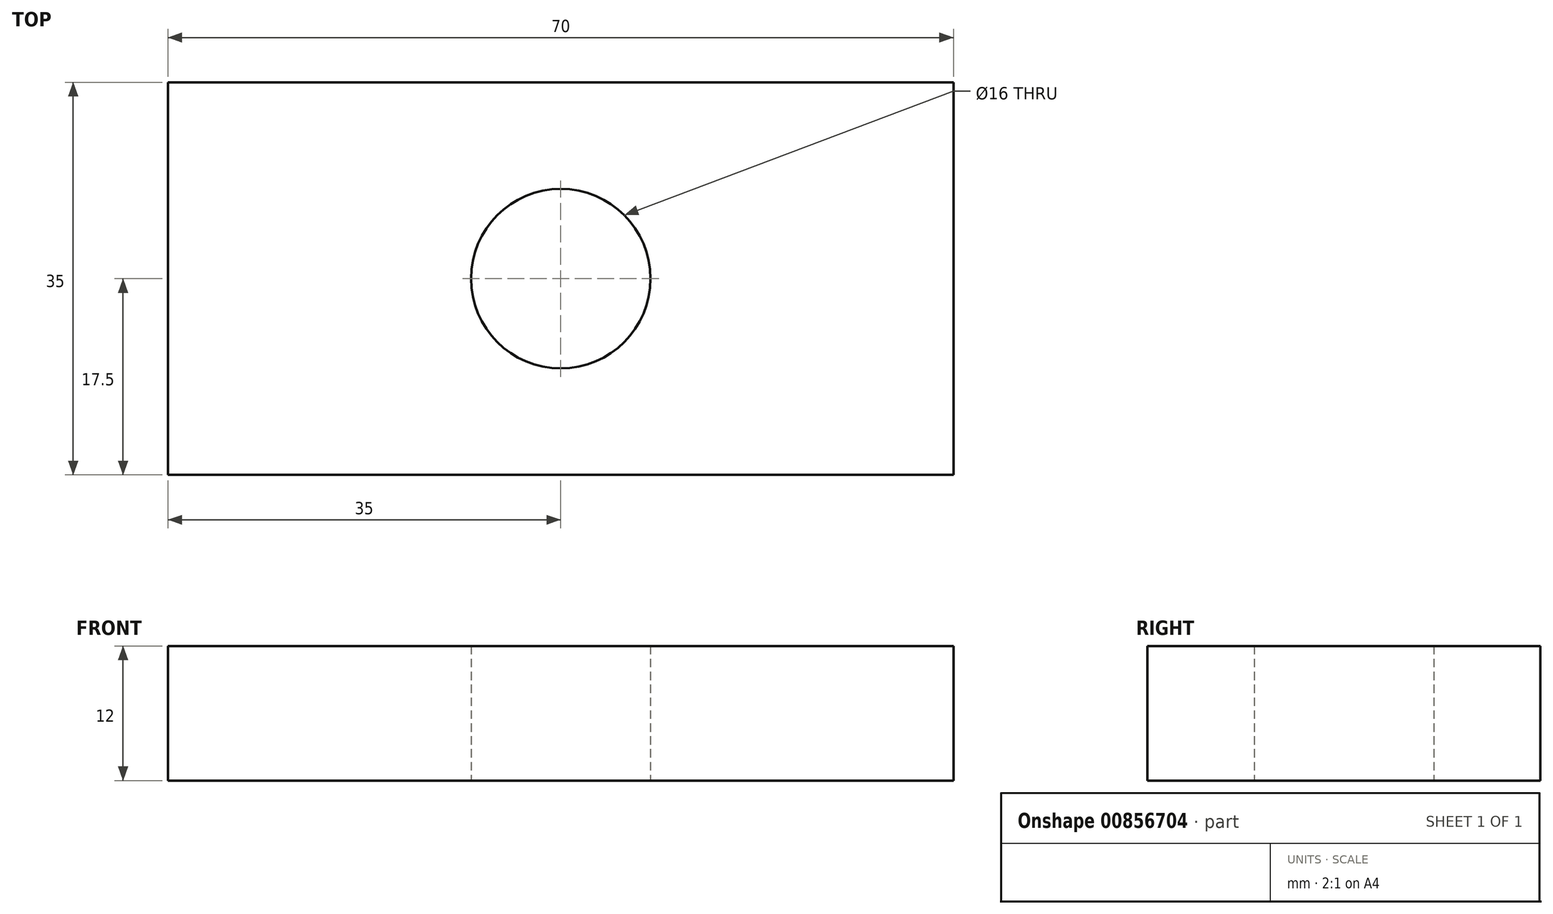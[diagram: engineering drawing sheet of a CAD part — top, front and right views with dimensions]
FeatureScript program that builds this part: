
annotation { "Feature Type Name" : "Feature", "Feature Type Description" : "" }
export const myFeature = defineFeature(function(context is Context, id is Id, definition is map)
    precondition{}
    {
        {
            var Q0;
            Q0=qCreatedBy(makeId("Top.planeOp"),FACE);
            var sketch = newSketch(context, id + "F0", { "sketchPlane" : qUnion([Q0])});
            skCircle(sketch, "E0", {"center": v(0, 0) * mm, "radius": 8 * mm});
            skLineSegment(sketch, "E1.bottom", {"start": v(-35, -17.5) * mm, "end": v(35, -17.5) * mm});
            skLineSegment(sketch, "E1.top", {"start": v(-35, 17.5) * mm, "end": v(35, 17.5) * mm});
            skLineSegment(sketch, "E1.left", {"start": v(-35, -17.5) * mm, "end": v(-35, 17.5) * mm});
            skLineSegment(sketch, "E1.right", {"start": v(35, -17.5) * mm, "end": v(35, 17.5) * mm});
            skLineSegment(sketch, "E2.bottom", {"start": v(-60, -25) * mm, "end": v(60, -25) * mm});
            skLineSegment(sketch, "E2.top", {"start": v(-60, 25) * mm, "end": v(60, 25) * mm});
            skLineSegment(sketch, "E2.left", {"start": v(-60, -25) * mm, "end": v(-60, -7.5) * mm});
            skLineSegment(sketch, "E2.right", {"start": v(60, -25) * mm, "end": v(60, -7.5) * mm});
            skArc(sketch, "E3", {"start": v(-60, -7.5) * mm, "mid": v(-52.5, 0) * mm, "end": v(-60, 7.5) * mm});
            skArc(sketch, "E4", {"start": v(60, 7.5) * mm, "mid": v(52.5, 0) * mm, "end": v(60, -7.5) * mm});
            skLineSegment(sketch, "E5.trimOffspring", {"start": v(-60, 7.5) * mm, "end": v(-60, 25) * mm});
            skLineSegment(sketch, "E6.trimOffspring", {"start": v(60, 7.5) * mm, "end": v(60, 25) * mm});
            skSolve(sketch);
        }
        {
            var Q0;
            Q0=makeQuery(id+"F0.imprint","IMPRINT",FACE,{"disambiguationData":[TD([[makeQuery(id+"F0.imprint","IMPRINT",EDGE,{"derivedFrom":sQuery(id+"F0.wireOp",EDGE,"E0")}),-1.0]])]});
            extrude(context, id + "F1", {"entities" : qUnion([Q0]), "depth" : 12 * mm, "offsetDistance" : 25 * mm});
        }
    });
